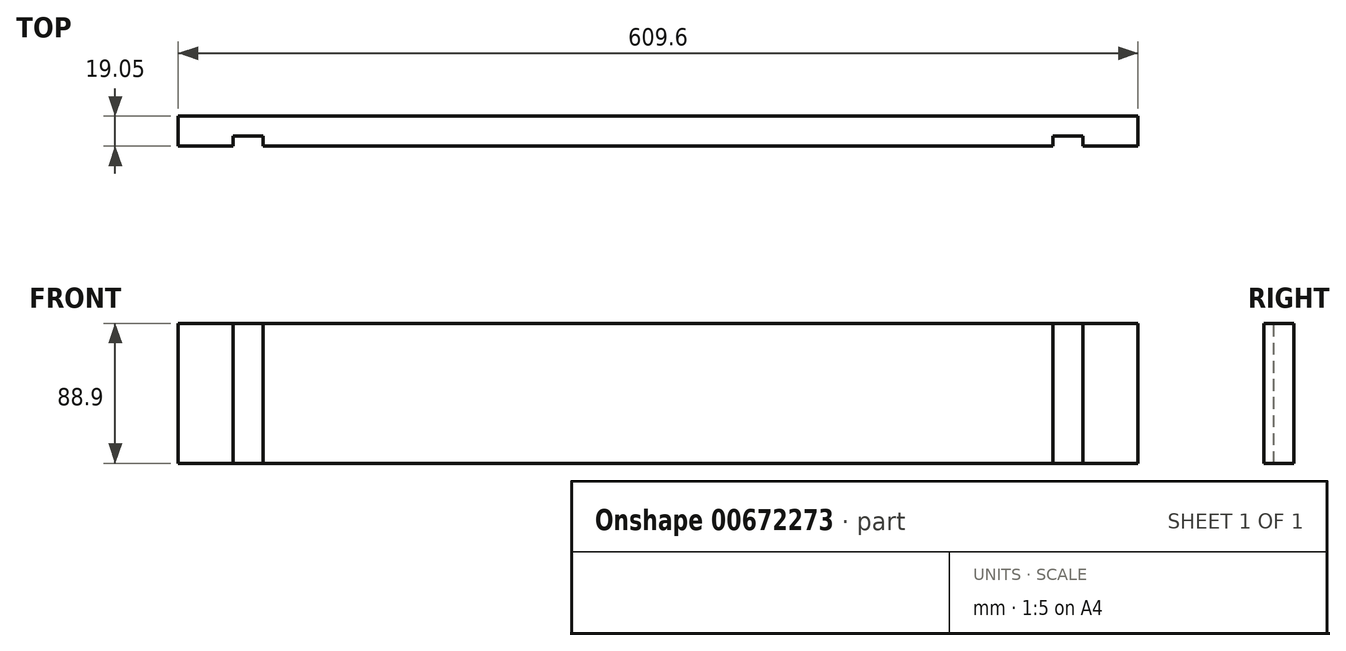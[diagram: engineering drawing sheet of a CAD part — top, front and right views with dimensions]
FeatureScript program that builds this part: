
annotation { "Feature Type Name" : "Feature", "Feature Type Description" : "" }
export const myFeature = defineFeature(function(context is Context, id is Id, definition is map)
    precondition{}
    {
        {
            var Q0;
            Q0=qCreatedBy(makeId("Front.planeOp"),FACE);
            var sketch = newSketch(context, id + "F0", { "sketchPlane" : qUnion([Q0])});
            skLineSegment(sketch, "E0.bottom", {"start": v(0, 88.9) * mm, "end": v(609.6, 88.9) * mm});
            skLineSegment(sketch, "E0.top", {"start": v(0, 0) * mm, "end": v(609.6, 0) * mm});
            skLineSegment(sketch, "E0.left", {"start": v(0, 88.9) * mm, "end": v(0, 0) * mm});
            skLineSegment(sketch, "E0.right", {"start": v(609.6, 88.9) * mm, "end": v(609.6, 0) * mm});
            skSolve(sketch);
        }
        {
            var Q0;
            Q0=makeQuery(id+"F0.imprint","IMPRINT",FACE,{"disambiguationData":[TD([[makeQuery(id+"F0.imprint","IMPRINT",EDGE,{"derivedFrom":sQuery(id+"F0.wireOp",EDGE,"E0.bottom")}),-1.0]])]});
            extrude(context, id + "F1", {"entities" : qUnion([Q0]), "depth" : 19.05 * mm, "offsetDistance" : 25.4 * mm});
        }
        {
            var Q0;
            Q0=makeQuery(id+"F1.opExtrude","SWEPT_FACE",FACE,{"disambiguationData":[OSD([sQuery(id+"F0.wireOp",EDGE,"E0.bottom")])]});
            var sketch = newSketch(context, id + "F2", { "sketchPlane" : qUnion([Q0])});
            skLineSegment(sketch, "E1.bottom", {"start": v(34.93, -19.05) * mm, "end": v(53.98, -19.05) * mm});
            skLineSegment(sketch, "E1.top", {"start": v(34.93, -12.7) * mm, "end": v(53.98, -12.7) * mm});
            skLineSegment(sketch, "E1.left", {"start": v(34.93, -19.05) * mm, "end": v(34.93, -12.7) * mm});
            skLineSegment(sketch, "E1.right", {"start": v(53.98, -19.05) * mm, "end": v(53.98, -12.7) * mm});
            skLineSegment(sketch, "E2.bottom", {"start": v(574.68, -19.05) * mm, "end": v(555.62, -19.05) * mm});
            skLineSegment(sketch, "E2.top", {"start": v(574.68, -12.7) * mm, "end": v(555.62, -12.7) * mm});
            skLineSegment(sketch, "E2.left", {"start": v(574.68, -19.05) * mm, "end": v(574.68, -12.7) * mm});
            skLineSegment(sketch, "E2.right", {"start": v(555.62, -19.05) * mm, "end": v(555.62, -12.7) * mm});
            skSolve(sketch);
        }
        {
            var Q0;
            Q0 = qSketchRegion(id + "F2", true);
            extrude(context, id + "F3", {"entities" : qUnion([Q0]), "operationType" : NewBodyOperationType.REMOVE, "endBound" : BoundingType.THROUGH_ALL, "oppositeDirection" : true, "depth" : 25.4 * mm, "offsetDistance" : 25.4 * mm});
        }
    });
